# Revit family: Lighting_Outside_Focus-Lighting_Dua-High
name_source: partatom
category: Lighting Fixtures
revit_build: Autodesk Revit 2018 (Build: 20190510_1515(x64)
units: mm (PartAtom-declared; Revit-internal decimal feet)

## family parameters
Always vertical = No
Cut with Voids When Loaded = No
Light Source = Yes
OmniClass Number = 23.35.47.23
OmniClass Title = Lamps
Part Type = Normal
Room Calculation Point = No
Round Connector Dimension = Use Diameter
Shared = No
Work Plane-Based = Yes

## types (1)
- Lighting_Outside_Focus-Lighting_Dua-High
    Always visible = Yes
    Anchors Material = Focus Lighting - Metal - Silver grey
    BIMobject category = Outside
    Color Filter = 16777215
    Default Elevation = 1219.2 mm  [stored 4 ft]
    Description = Dua High by Juul Frost Architects is minimalist in its slim, cylindrical form. Available with single or double-sided light slit.
    Design country = Denmark
    Dimming Lamp Color Temperature Shift = <None>
    Double = Yes
    Edition number = 1
    Manufacturer = Focus Lighting
    Manufacturer country = Denmark
    Manufacturer name = Focus Lighting
    Material main = Aluminium
    Material secondary = Polycarbonate
    Model = Dua High
    Photometric Web File = Dua High Double_827.IES
    Product Guid = 021d0059-e8fc-40bc-9862-2f0c9af896f5
    Product SKU = dua-high
    Product data url = https://bimobject.com
    Product family = Outdoor
    Product group = Columns
    Product name = Dua High
    Product url = https://www.focus-lighting.dk
    QR code = https://bimobject.com
    Shade material = Focus Lighting - Glass - Glass
    Single = No
    Tilt Angle = 90.00°
    URL = https://www.focus-lighting.dk
    Voltage = 230 V
    Weight Net (Kg) = 15

note: [stored X ft] marks values corroborated as IEEE doubles in the binary element streams (Revit-internal decimal feet)

## geometry (parser evidence)
native form markers: Sweep x2
no freeform markers — native parametric forms only
